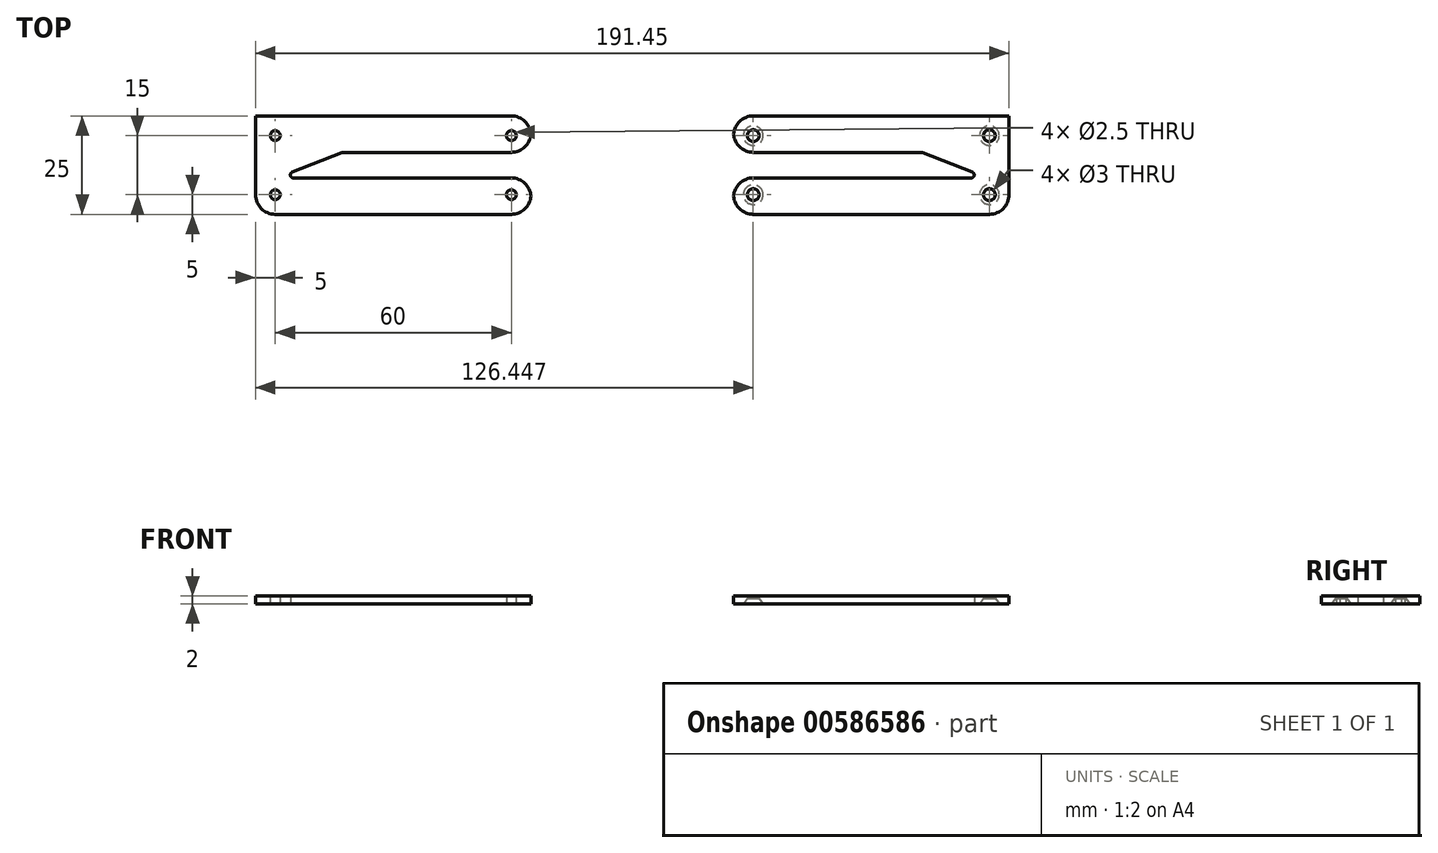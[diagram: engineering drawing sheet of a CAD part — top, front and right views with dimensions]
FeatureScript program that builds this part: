
annotation { "Feature Type Name" : "Feature", "Feature Type Description" : "" }
export const myFeature = defineFeature(function(context is Context, id is Id, definition is map)
    precondition{}
    {
        {
            var Q0;
            Q0=qCreatedBy(makeId("Top.planeOp"),FACE);
            var sketch = newSketch(context, id + "F0", { "sketchPlane" : qUnion([Q0])});
            skLineSegment(sketch, "E0.bottom", {"start": v(-35, -12.5) * mm, "end": v(35, -12.5) * mm});
            skLineSegment(sketch, "E0.top", {"start": v(-35, 12.5) * mm, "end": v(35, 12.5) * mm});
            skLineSegment(sketch, "E0.left", {"start": v(-35, -12.5) * mm, "end": v(-35, 12.5) * mm});
            skLineSegment(sketch, "E0.right", {"start": v(35, -12.5) * mm, "end": v(35, 12.5) * mm});
            skPoint(sketch, "E0.middle", {"position": v(0, 0) * mm});
            skLineSegment(sketch, "E1", {"start": v(0, 2.5) * mm, "end": v(0, -2.5) * mm});
            skLineSegment(sketch, "E2", {"start": v(-25.4, -2.5) * mm, "end": v(25.4, -2.5) * mm});
            skLineSegment(sketch, "E3", {"start": v(-12.7, 2.5) * mm, "end": v(12.7, 2.5) * mm});
            skLineSegment(sketch, "E4", {"start": v(25.4, -2.5) * mm, "end": v(50.2, -2.5) * mm});
            skLineSegment(sketch, "E5", {"start": v(-25.4, -2.5) * mm, "end": v(-12.7, 2.5) * mm});
            skLineSegment(sketch, "E6", {"start": v(12.7, 2.5) * mm, "end": v(45.79, 2.5) * mm});
            skArc(sketch, "E7.0.startCap", {"start": v(12.7, 1.75) * mm, "mid": v(11.95, 2.5) * mm, "end": v(12.7, 3.25) * mm});
            skArc(sketch, "E7.0.endCap", {"start": v(45.79, 3.25) * mm, "mid": v(46.54, 2.5) * mm, "end": v(45.79, 1.75) * mm});
            skLineSegment(sketch, "E7.0.left", {"start": v(12.7, 3.25) * mm, "end": v(45.79, 3.25) * mm});
            skLineSegment(sketch, "E7.0.right", {"start": v(12.7, 1.75) * mm, "end": v(45.79, 1.75) * mm});
            skArc(sketch, "E7.1.startCap", {"start": v(-12.7, 1.75) * mm, "mid": v(-13.45, 2.5) * mm, "end": v(-12.7, 3.25) * mm});
            skArc(sketch, "E7.1.endCap", {"start": v(12.7, 3.25) * mm, "mid": v(13.45, 2.5) * mm, "end": v(12.7, 1.75) * mm});
            skLineSegment(sketch, "E7.1.left", {"start": v(-12.7, 3.25) * mm, "end": v(12.7, 3.25) * mm});
            skLineSegment(sketch, "E7.1.right", {"start": v(-12.7, 1.75) * mm, "end": v(12.7, 1.75) * mm});
            skArc(sketch, "E7.2.startCap", {"start": v(-25.13, -3.2) * mm, "mid": v(-26.1, -2.77) * mm, "end": v(-25.67, -1.8) * mm});
            skArc(sketch, "E7.2.endCap", {"start": v(-12.97, 3.2) * mm, "mid": v(-12, 2.77) * mm, "end": v(-12.43, 1.8) * mm});
            skLineSegment(sketch, "E7.2.left", {"start": v(-25.67, -1.8) * mm, "end": v(-12.97, 3.2) * mm});
            skLineSegment(sketch, "E7.2.right", {"start": v(-25.13, -3.2) * mm, "end": v(-12.43, 1.8) * mm});
            skArc(sketch, "E7.3.startCap", {"start": v(-25.4, -3.25) * mm, "mid": v(-26.15, -2.5) * mm, "end": v(-25.4, -1.75) * mm});
            skArc(sketch, "E7.3.endCap", {"start": v(25.4, -1.75) * mm, "mid": v(26.15, -2.5) * mm, "end": v(25.4, -3.25) * mm});
            skLineSegment(sketch, "E7.3.left", {"start": v(-25.4, -1.75) * mm, "end": v(25.4, -1.75) * mm});
            skLineSegment(sketch, "E7.3.right", {"start": v(-25.4, -3.25) * mm, "end": v(25.4, -3.25) * mm});
            skArc(sketch, "E7.4.startCap", {"start": v(25.4, -3.25) * mm, "mid": v(24.65, -2.5) * mm, "end": v(25.4, -1.75) * mm});
            skArc(sketch, "E7.4.endCap", {"start": v(50.2, -1.75) * mm, "mid": v(50.95, -2.5) * mm, "end": v(50.2, -3.25) * mm});
            skLineSegment(sketch, "E7.4.left", {"start": v(25.4, -1.75) * mm, "end": v(50.2, -1.75) * mm});
            skLineSegment(sketch, "E7.4.right", {"start": v(25.4, -3.25) * mm, "end": v(50.2, -3.25) * mm});
            skPoint(sketch, "E8", {"position": v(-30, 7.5) * mm});
            skPoint(sketch, "E9", {"position": v(-30, -7.5) * mm});
            skPoint(sketch, "E10", {"position": v(30, -7.5) * mm});
            skPoint(sketch, "E11", {"position": v(30, 7.5) * mm});
            skLineSegment(sketch, "E12", {"start": v(-35, 12.5) * mm, "end": v(-30, 12.5) * mm});
            skLineSegment(sketch, "E13", {"start": v(-30, 12.5) * mm, "end": v(-35, 12.5) * mm});
            skLineSegment(sketch, "E14", {"start": v(-35, 12.5) * mm, "end": v(-35, 7.5) * mm});
            skLineSegment(sketch, "E15", {"start": v(-35, -12.5) * mm, "end": v(-35, -7.5) * mm});
            skLineSegment(sketch, "E16", {"start": v(35, -12.5) * mm, "end": v(30, -12.5) * mm});
            skLineSegment(sketch, "E17", {"start": v(60.72, 22.29) * mm, "end": v(60.72, -29.52) * mm});
            skArc(sketch, "E18.MirrorCS", {"start": v(108.75, 3.25) * mm, "mid": v(108, 2.5) * mm, "end": v(108.75, 1.75) * mm});
            skArc(sketch, "E19.MirrorCS", {"start": v(96.05, -1.75) * mm, "mid": v(95.3, -2.5) * mm, "end": v(96.05, -3.25) * mm});
            skArc(sketch, "E20.MirrorCS", {"start": v(146.57, -3.2) * mm, "mid": v(147.54, -2.77) * mm, "end": v(147.12, -1.8) * mm});
            skArc(sketch, "E21.MirrorCS", {"start": v(96.05, -3.25) * mm, "mid": v(96.8, -2.5) * mm, "end": v(96.05, -1.75) * mm});
            skArc(sketch, "E22.MirrorCS", {"start": v(146.85, -3.25) * mm, "mid": v(147.6, -2.5) * mm, "end": v(146.85, -1.75) * mm});
            skArc(sketch, "E23.MirrorCS", {"start": v(134.42, 3.2) * mm, "mid": v(133.45, 2.77) * mm, "end": v(133.87, 1.8) * mm});
            skArc(sketch, "E24.MirrorCS", {"start": v(75.66, 3.25) * mm, "mid": v(74.9, 2.5) * mm, "end": v(75.66, 1.75) * mm});
            skArc(sketch, "E25.MirrorCS", {"start": v(134.15, 1.75) * mm, "mid": v(134.9, 2.5) * mm, "end": v(134.15, 3.25) * mm});
            skArc(sketch, "E26.MirrorCS", {"start": v(108.75, 1.75) * mm, "mid": v(109.5, 2.5) * mm, "end": v(108.75, 3.25) * mm});
            skArc(sketch, "E27.MirrorCS", {"start": v(71.25, -1.75) * mm, "mid": v(70.5, -2.5) * mm, "end": v(71.25, -3.25) * mm});
            skLineSegment(sketch, "E28.MirrorCS", {"start": v(121.45, 2.5) * mm, "end": v(121.45, -2.5) * mm});
            skLineSegment(sketch, "E29.MirrorCS", {"start": v(156.45, 12.5) * mm, "end": v(151.45, 12.5) * mm});
            skPoint(sketch, "E30.MirrorP", {"position": v(151.45, 7.5) * mm});
            skLineSegment(sketch, "E31.MirrorCS", {"start": v(108.75, 1.75) * mm, "end": v(75.66, 1.75) * mm});
            skLineSegment(sketch, "E32.MirrorCS", {"start": v(108.75, 3.25) * mm, "end": v(75.66, 3.25) * mm});
            skPoint(sketch, "E33.MirrorP", {"position": v(91.45, 7.5) * mm});
            skLineSegment(sketch, "E34.MirrorCS", {"start": v(134.15, 2.5) * mm, "end": v(108.75, 2.5) * mm});
            skLineSegment(sketch, "E35.MirrorCS", {"start": v(86.45, -12.5) * mm, "end": v(91.45, -12.5) * mm});
            skLineSegment(sketch, "E36.MirrorCS", {"start": v(156.45, -12.5) * mm, "end": v(156.45, 12.5) * mm});
            skLineSegment(sketch, "E37.MirrorCS", {"start": v(108.75, 2.5) * mm, "end": v(75.66, 2.5) * mm});
            skPoint(sketch, "E38.MirrorP", {"position": v(151.45, -7.5) * mm});
            skLineSegment(sketch, "E39.MirrorCS", {"start": v(156.45, 12.5) * mm, "end": v(156.45, 7.5) * mm});
            skLineSegment(sketch, "E40.MirrorCS", {"start": v(156.45, 12.5) * mm, "end": v(86.45, 12.5) * mm});
            skLineSegment(sketch, "E41.MirrorCS", {"start": v(96.05, -2.5) * mm, "end": v(71.25, -2.5) * mm});
            skPoint(sketch, "E42.MirrorP", {"position": v(91.45, -7.5) * mm});
            skPoint(sketch, "E43.MirrorP", {"position": v(121.45, 0) * mm});
            skLineSegment(sketch, "E44.MirrorCS", {"start": v(156.45, -12.5) * mm, "end": v(86.45, -12.5) * mm});
            skLineSegment(sketch, "E45.MirrorCS", {"start": v(146.57, -3.2) * mm, "end": v(133.87, 1.8) * mm});
            skLineSegment(sketch, "E46.MirrorCS", {"start": v(151.45, 12.5) * mm, "end": v(156.45, 12.5) * mm});
            skLineSegment(sketch, "E47.MirrorCS", {"start": v(146.85, -3.25) * mm, "end": v(96.05, -3.25) * mm});
            skLineSegment(sketch, "E48.MirrorCS", {"start": v(96.05, -1.75) * mm, "end": v(71.25, -1.75) * mm});
            skLineSegment(sketch, "E49.MirrorCS", {"start": v(146.85, -2.5) * mm, "end": v(96.05, -2.5) * mm});
            skLineSegment(sketch, "E50.MirrorCS", {"start": v(96.05, -3.25) * mm, "end": v(71.25, -3.25) * mm});
            skLineSegment(sketch, "E51.MirrorCS", {"start": v(134.15, 1.75) * mm, "end": v(108.75, 1.75) * mm});
            skLineSegment(sketch, "E52.MirrorCS", {"start": v(146.85, -1.75) * mm, "end": v(96.05, -1.75) * mm});
            skLineSegment(sketch, "E53.MirrorCS", {"start": v(147.12, -1.8) * mm, "end": v(134.42, 3.2) * mm});
            skLineSegment(sketch, "E54.MirrorCS", {"start": v(86.45, -12.5) * mm, "end": v(86.45, 12.5) * mm});
            skLineSegment(sketch, "E55.MirrorCS", {"start": v(156.45, -12.5) * mm, "end": v(156.45, -7.5) * mm});
            skLineSegment(sketch, "E56.MirrorCS", {"start": v(146.85, -2.5) * mm, "end": v(134.15, 2.5) * mm});
            skLineSegment(sketch, "E57.MirrorCS", {"start": v(134.15, 3.25) * mm, "end": v(108.75, 3.25) * mm});
            skSolve(sketch);
        }
        {
            var Q0;
            Q0=makeQuery(id+"F0.imprint","IMPRINT",FACE,{"disambiguationData":[TD([[makeQuery(id+"F0.imprint","IMPRINT",EDGE,{"derivedFrom":sQuery(id+"F0.wireOp",EDGE,"E0.bottom")}),1.0]])]});
            var Q1;
            Q1=makeQuery(id+"F0.imprint","IMPRINT",FACE,{"disambiguationData":[TD([[makeQuery(id+"F0.imprint","IMPRINT",EDGE,{"derivedFrom":sQuery(id+"F0.wireOp",EDGE,"E36.MirrorCS")}),1.0]])]});
            extrude(context, id + "F1", {"entities" : qUnion([Q0, Q1]), "depth" : 2 * mm, "offsetDistance" : 25.4 * mm});
        }
        {
            var Q0;
            Q0=makeQuery(id+"F1.opExtrude","SWEPT_EDGE",EDGE,{"disambiguationData":[OSD([sQuery(id+"F0.wireOp",EDGE,"E13"),sQuery(id+"F0.wireOp",EDGE,"E14")])]});
            var Q1;
            Q1=makeQuery(id+"F1.opExtrude","SWEPT_EDGE",EDGE,{"disambiguationData":[OSD([sQuery(id+"F0.wireOp",EDGE,"E0.top"),sQuery(id+"F0.wireOp",EDGE,"E0.right")])]});
            var Q2;
            Q2=makeQuery(id+"F1.opExtrude","SWEPT_EDGE",EDGE,{"disambiguationData":[OSD([sQuery(id+"F0.wireOp",EDGE,"E0.bottom"),sQuery(id+"F0.wireOp",EDGE,"E15")])]});
            var Q3;
            Q3=makeQuery(id+"F1.opExtrude","SWEPT_EDGE",EDGE,{"disambiguationData":[OSD([sQuery(id+"F0.wireOp",EDGE,"E0.right"),sQuery(id+"F0.wireOp",EDGE,"E16")])]});
            var Q4;
            Q4=makeQuery(id+"F1.opExtrude","SWEPT_EDGE",EDGE,{"disambiguationData":[OSD([sQuery(id+"F0.wireOp",EDGE,"E40.MirrorCS"),sQuery(id+"F0.wireOp",EDGE,"E54.MirrorCS")])]});
            var Q5;
            Q5=makeQuery(id+"F1.opExtrude","SWEPT_EDGE",EDGE,{"disambiguationData":[OSD([sQuery(id+"F0.wireOp",EDGE,"E39.MirrorCS"),sQuery(id+"F0.wireOp",EDGE,"E46.MirrorCS")])]});
            var Q6;
            Q6=makeQuery(id+"F1.opExtrude","SWEPT_EDGE",EDGE,{"disambiguationData":[OSD([sQuery(id+"F0.wireOp",EDGE,"E44.MirrorCS"),sQuery(id+"F0.wireOp",EDGE,"E54.MirrorCS")])]});
            var Q7;
            Q7=makeQuery(id+"F1.opExtrude","SWEPT_EDGE",EDGE,{"disambiguationData":[OSD([sQuery(id+"F0.wireOp",EDGE,"E44.MirrorCS"),sQuery(id+"F0.wireOp",EDGE,"E55.MirrorCS")])]});
            fillet(context, id + "F2", {"entities" : qUnion([Q0, Q1, Q2, Q3, Q4, Q5, Q6, Q7]), "radius" : 5 * mm, "tangentPropagation" : true, "allowEdgeOverflow" : false});
        }
        {
            var Q0;
            Q0=sQuery(id+"F0.wireOp",VERTEX,"E8");
            var Q1;
            Q1=sQuery(id+"F0.wireOp",VERTEX,"E9");
            var Q2;
            Q2=sQuery(id+"F0.wireOp",VERTEX,"E10");
            var Q3;
            Q3=sQuery(id+"F0.wireOp",VERTEX,"E11");
            var Q4;
            Q4=makeQuery(id+"F1.opExtrude","SWEPT_BODY",BODY,{"disambiguationData":[OSD([sQuery(id+"F0.wireOp",EDGE,"E0.bottom"),sQuery(id+"F0.wireOp",EDGE,"E0.top"),sQuery(id+"F0.wireOp",EDGE,"E0.left"),sQuery(id+"F0.wireOp",EDGE,"E0.right"),sQuery(id+"F0.wireOp",EDGE,"E7.0.left"),sQuery(id+"F0.wireOp",EDGE,"E7.1.left"),sQuery(id+"F0.wireOp",EDGE,"E7.2.endCap"),sQuery(id+"F0.wireOp",EDGE,"E7.2.left"),sQuery(id+"F0.wireOp",EDGE,"E7.3.startCap"),sQuery(id+"F0.wireOp",EDGE,"E7.3.right"),sQuery(id+"F0.wireOp",EDGE,"E7.4.right"),sQuery(id+"F0.wireOp",EDGE,"E13"),sQuery(id+"F0.wireOp",EDGE,"E14"),sQuery(id+"F0.wireOp",EDGE,"E15"),sQuery(id+"F0.wireOp",EDGE,"E16")])]});
            hole(context, id + "F3", {"style" : HoleStyle.SIMPLE, "endStyle" : HoleEndStyle.THROUGH, "oppositeDirection" : true, "holeDiameter" : 2.5 * mm, "majorDiameter" : 5 * mm, "isTappedThrough" : true, "tappedDepth" : 12 * mm, "tapClearance" : 3, "locations" : qUnion([Q0, Q1, Q2, Q3]), "scope" : qUnion([Q4])});
        }
        {
            var Q0;
            Q0=sQuery(id+"F0.wireOp",VERTEX,"E33.MirrorP");
            var Q1;
            Q1=sQuery(id+"F0.wireOp",VERTEX,"E30.MirrorP");
            var Q2;
            Q2=sQuery(id+"F0.wireOp",VERTEX,"E38.MirrorP");
            var Q3;
            Q3=sQuery(id+"F0.wireOp",VERTEX,"E42.MirrorP");
            var Q4;
            Q4=makeQuery(id+"F1.opExtrude","SWEPT_BODY",BODY,{"disambiguationData":[OSD([sQuery(id+"F0.wireOp",EDGE,"E22.MirrorCS"),sQuery(id+"F0.wireOp",EDGE,"E25.MirrorCS"),sQuery(id+"F0.wireOp",EDGE,"E32.MirrorCS"),sQuery(id+"F0.wireOp",EDGE,"E36.MirrorCS"),sQuery(id+"F0.wireOp",EDGE,"E39.MirrorCS"),sQuery(id+"F0.wireOp",EDGE,"E40.MirrorCS"),sQuery(id+"F0.wireOp",EDGE,"E44.MirrorCS"),sQuery(id+"F0.wireOp",EDGE,"E46.MirrorCS"),sQuery(id+"F0.wireOp",EDGE,"E47.MirrorCS"),sQuery(id+"F0.wireOp",EDGE,"E50.MirrorCS"),sQuery(id+"F0.wireOp",EDGE,"E53.MirrorCS"),sQuery(id+"F0.wireOp",EDGE,"E54.MirrorCS"),sQuery(id+"F0.wireOp",EDGE,"E55.MirrorCS"),sQuery(id+"F0.wireOp",EDGE,"E57.MirrorCS")])]});
            hole(context, id + "F4", {"style" : HoleStyle.C_SINK, "endStyle" : HoleEndStyle.THROUGH, "oppositeDirection" : true, "holeDiameter" : 3 * mm, "cSinkDiameter" : 5 * mm, "cSinkAngle" : 70 * degree, "majorDiameter" : 5 * mm, "isTappedThrough" : true, "tappedDepth" : 12 * mm, "tapClearance" : 3, "locations" : qUnion([Q0, Q1, Q2, Q3]), "scope" : qUnion([Q4])});
        }
    });
